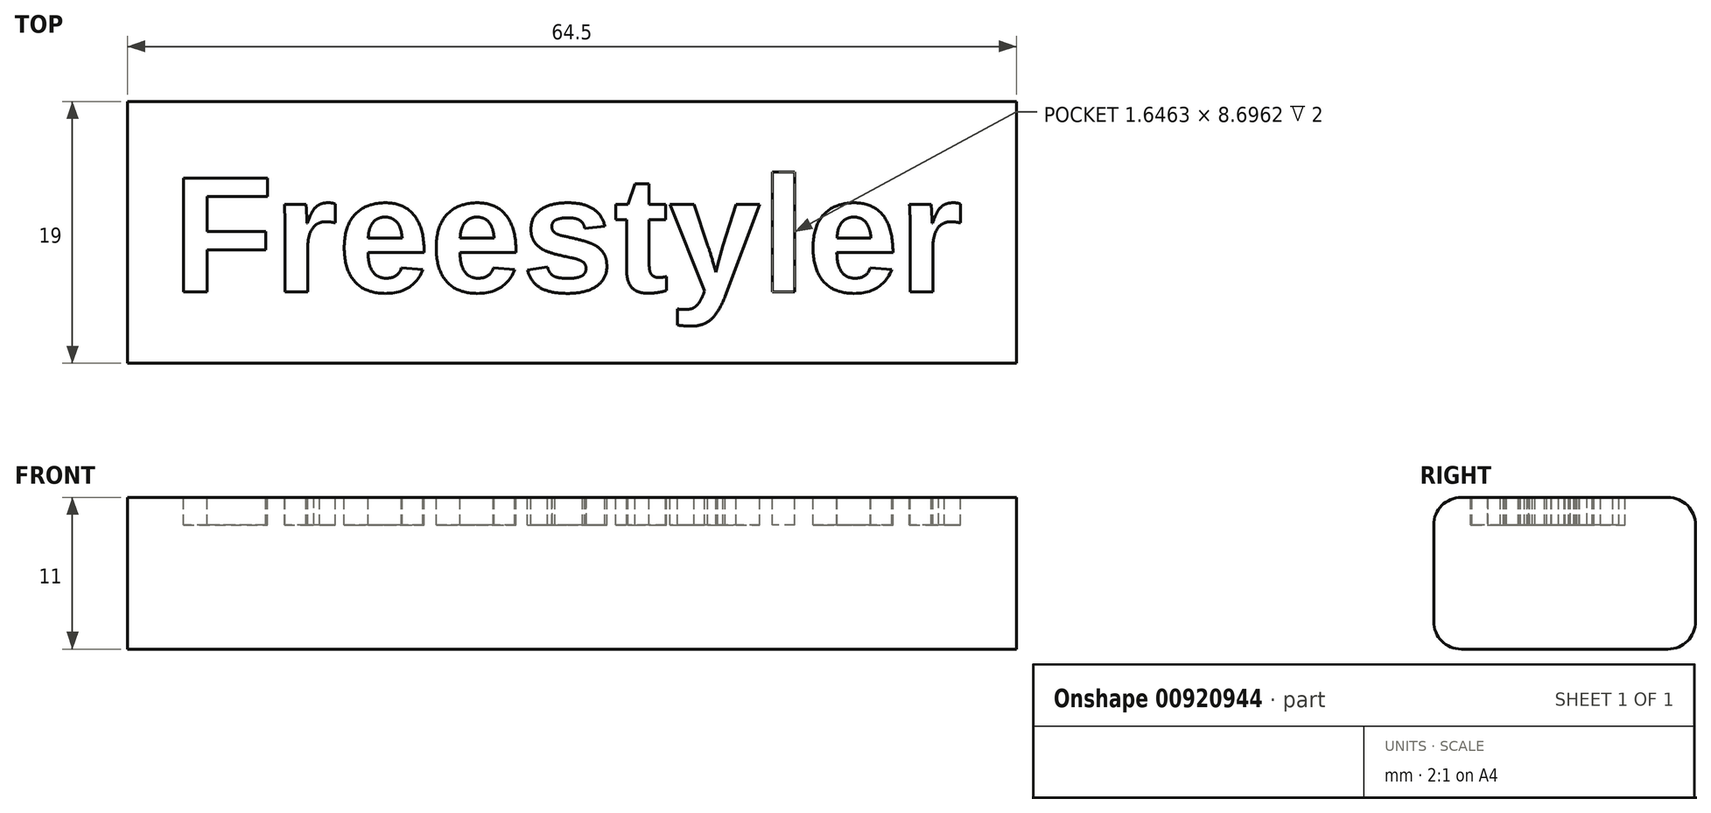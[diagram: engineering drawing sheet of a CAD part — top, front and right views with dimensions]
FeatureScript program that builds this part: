
annotation { "Feature Type Name" : "Feature", "Feature Type Description" : "" }
export const myFeature = defineFeature(function(context is Context, id is Id, definition is map)
    precondition{}
    {
        {
            var Q0;
            Q0=qCreatedBy(makeId("Top.planeOp"),FACE);
            var sketch = newSketch(context, id + "F0", { "sketchPlane" : qUnion([Q0])});
            skLineSegment(sketch, "E0.bottom", {"start": v(-32.25, 9.5) * mm, "end": v(32.25, 9.5) * mm});
            skLineSegment(sketch, "E0.top", {"start": v(-32.25, -9.5) * mm, "end": v(32.25, -9.5) * mm});
            skLineSegment(sketch, "E0.left", {"start": v(-32.25, 9.5) * mm, "end": v(-32.25, -9.5) * mm});
            skLineSegment(sketch, "E0.right", {"start": v(32.25, 9.5) * mm, "end": v(32.25, -9.5) * mm});
            skSolve(sketch);
        }
        {
            var Q0;
            Q0=makeQuery(id+"F0.imprint","IMPRINT",FACE,{"disambiguationData":[TD([[makeQuery(id+"F0.imprint","IMPRINT",EDGE,{"derivedFrom":sQuery(id+"F0.wireOp",EDGE,"E0.bottom")}),-1.0]])]});
            extrude(context, id + "F1", {"entities" : qUnion([Q0]), "depth" : 11 * mm, "offsetDistance" : 25 * mm});
        }
        {
            var Q0;
            Q0=makeQuery(id+"F1.opExtrude","CAP_EDGE",EDGE,{"disambiguationData":[OSD([sQuery(id+"F0.wireOp",EDGE,"E0.bottom")])],"isStart":false});
            var Q1;
            Q1=makeQuery(id+"F1.opExtrude","CAP_EDGE",EDGE,{"disambiguationData":[OSD([sQuery(id+"F0.wireOp",EDGE,"E0.top")])],"isStart":false});
            var Q2;
            Q2=makeQuery(id+"F1.opExtrude","CAP_EDGE",EDGE,{"disambiguationData":[OSD([sQuery(id+"F0.wireOp",EDGE,"E0.top")])],"isStart":true});
            var Q3;
            Q3=makeQuery(id+"F1.opExtrude","CAP_EDGE",EDGE,{"disambiguationData":[OSD([sQuery(id+"F0.wireOp",EDGE,"E0.bottom")])],"isStart":true});
            fillet(context, id + "F2", {"entities" : qUnion([Q0, Q1, Q2, Q3]), "radius" : 2 * mm, "tangentPropagation" : true, "allowEdgeOverflow" : false});
        }
        {
            var Q0;
            Q0=makeQuery(id+"F1.opExtrude","CAP_FACE",FACE,{"disambiguationData":[OSD([sQuery(id+"F0.wireOp",EDGE,"E0.bottom"),sQuery(id+"F0.wireOp",EDGE,"E0.top"),sQuery(id+"F0.wireOp",EDGE,"E0.left"),sQuery(id+"F0.wireOp",EDGE,"E0.right")])],"isStart":false});
            var sketch = newSketch(context, id + "F3", { "sketchPlane" : qUnion([Q0])});
            skText(sketch, "E1", { "text": "Freestyler", "fontName": "Arimo-Bold.ttf"});
            const initialGuessF3  = {"E1": [-0.029, -0.00432, 1, 0, 0.00864]};
            skSetInitialGuess(sketch, initialGuessF3);
            skSolve(sketch);
        }
        {
            var Q0;
            Q0 = qSketchRegion(id + "F3", true);
            extrude(context, id + "F4", {"entities" : qUnion([Q0]), "operationType" : NewBodyOperationType.REMOVE, "oppositeDirection" : true, "depth" : 2 * mm, "offsetDistance" : 25 * mm});
        }
    });
